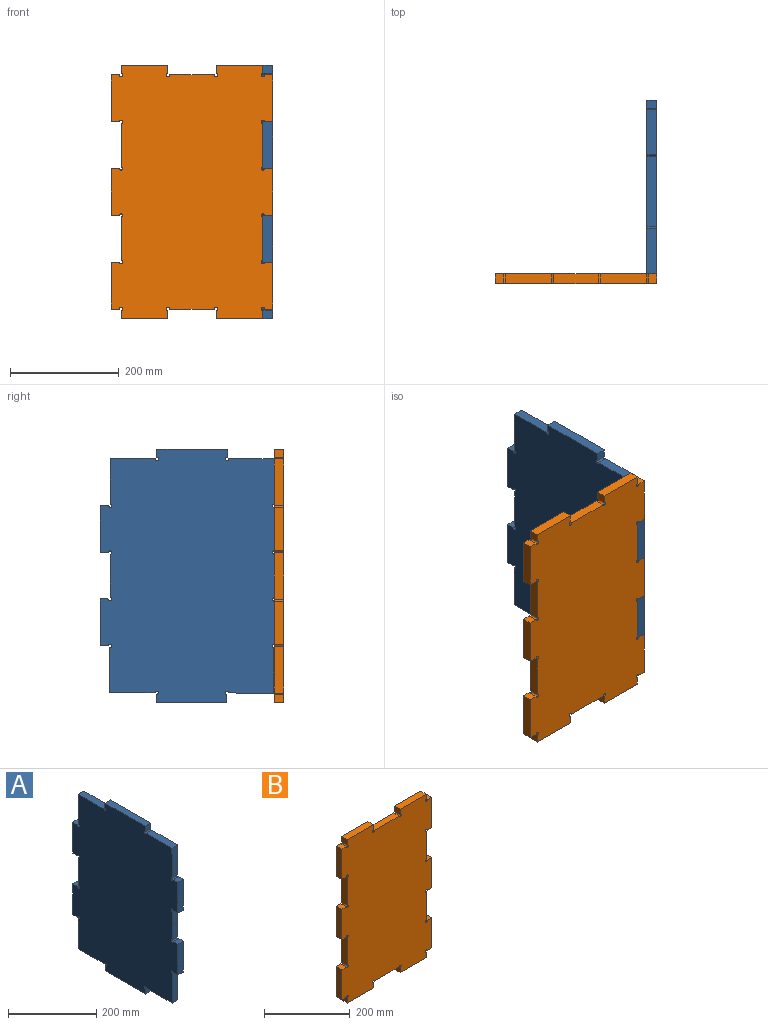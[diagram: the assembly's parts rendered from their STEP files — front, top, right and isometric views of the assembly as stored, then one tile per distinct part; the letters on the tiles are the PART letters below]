
ASSEMBLY  parts=2 mates=1
PART A: 44 faces, bbox 18x337.3x465.8 mm
  f0: plane 18x15mm, normal (0,0,1), area 270mm2, adj f24,f30,f31,f35
  f1: plane 39.62x18mm, normal (0,1,0), area 713.2mm2, adj f2,f24,f31,f35
  f2: plane 39.62x18mm, normal (0,1,0), area 713.2mm2, adj f1,f24,f31,f36
  f3: plane 18x15mm, normal (0,0,-1), area 270mm2, adj f24,f25,f31,f36
  f4: plane 18x15mm, normal (0,0,1), area 270mm2, adj f24,f25,f31,f37
  f5: plane 83x18mm, normal (0,1,0), area 1494mm2, adj f6,f24,f31,f37
  f6: plane 83x18mm, normal (0,0,1), area 1494mm2, adj f5,f24,f31,f38
  f7: plane 18x15mm, normal (0,1,0), area 270mm2, adj f24,f26,f31,f38
  f8: plane 18x15mm, normal (0,-1,0), area 270mm2, adj f24,f26,f31,f32
  f9: plane 83x18mm, normal (0,0,1), area 1494mm2, adj f10,f24,f31,f32
  f10: plane 83x18mm, normal (0,-1,0), area 1494mm2, adj f9,f24,f31,f43
  f11: plane 18x15mm, normal (0,0,1), area 270mm2, adj f24,f27,f31,f43
  f12: plane 18x15mm, normal (0,0,-1), area 270mm2, adj f24,f27,f31,f42
  f13: plane 40x18mm, normal (0,-1,0), area 720mm2, adj f14,f24,f31,f42
  f14: plane 40x18mm, normal (0,-1,0), area 720mm2, adj f13,f24,f31,f41
  f15: plane 18x15mm, normal (0,0,1), area 270mm2, adj f24,f28,f31,f41
  f16: plane 18x15mm, normal (0,0,-1), area 270mm2, adj f24,f28,f31,f40
  f17: plane 83x18mm, normal (0,-1,0), area 1494mm2, adj f18,f24,f31,f40
  f18: plane 83x18mm, normal (0,0,-1), area 1494mm2, adj f17,f24,f31,f39
  f19: plane 18x15mm, normal (0,-1,0), area 270mm2, adj f24,f29,f31,f39
  f20: plane 18x15mm, normal (0,1,0), area 270mm2, adj f24,f29,f31,f33
  f21: plane 83x18mm, normal (0,0,-1), area 1494mm2, adj f22,f24,f31,f33
  f22: plane 83x18mm, normal (0,1,0), area 1494mm2, adj f21,f24,f31,f34
  f23: plane 18x15mm, normal (0,0,-1), area 270mm2, adj f24,f30,f31,f34
  f24: plane 465.78x337.32mm, normal (1,0,0), area 139897.5mm2, adj f0,f1,f2,f3,f4,f5,f6,f7
  f25: plane 86x18mm, normal (0,1,0), area 1548mm2, adj f3,f4,f24,f31
  f26: plane 129x18mm, normal (0,0,1), area 2322mm2, adj f7,f8,f24,f31
  f27: plane 86x18mm, normal (0,-1,0), area 1548mm2, adj f11,f12,f24,f31
  f28: plane 86x18mm, normal (0,-1,0), area 1548mm2, adj f15,f16,f24,f31
  f29: plane 129x18mm, normal (0,0,-1), area 2322mm2, adj f19,f20,f24,f31
  f30: plane 86x18mm, normal (0,1,0), area 1548mm2, adj f0,f23,f24,f31
  f31: plane 465.78x337.32mm, normal (-1,0,0), area 139897.5mm2, adj f0,f1,f2,f3,f4,f5,f6,f7
  f32: cylinder r=3mm len=18mm, axis (1,0,0), area 254.5mm2, adj f8,f9,f24,f31
  f33: cylinder r=3mm len=18mm, axis (1,0,0), area 254.5mm2, adj f20,f21,f24,f31
  f34: cylinder r=3mm len=18mm, axis (1,0,0), area 254.5mm2, adj f22,f23,f24,f31
  f35: cylinder r=3mm len=18mm, axis (1,0,0), area 254.5mm2, adj f0,f1,f24,f31
  f36: cylinder r=3mm len=18mm, axis (1,0,0), area 254.5mm2, adj f2,f3,f24,f31
  f37: cylinder r=3mm len=18mm, axis (1,0,0), area 254.5mm2, adj f4,f5,f24,f31
  f38: cylinder r=3mm len=18mm, axis (1,0,0), area 254.5mm2, adj f6,f7,f24,f31
  f39: cylinder r=3mm len=18mm, axis (1,0,0), area 254.5mm2, adj f18,f19,f24,f31
  f40: cylinder r=3mm len=18mm, axis (1,0,0), area 254.5mm2, adj f16,f17,f24,f31
  f41: cylinder r=3mm len=18mm, axis (1,0,0), area 254.5mm2, adj f14,f15,f24,f31
  f42: cylinder r=3mm len=18mm, axis (1,0,0), area 254.5mm2, adj f12,f13,f24,f31
  f43: cylinder r=3mm len=18mm, axis (1,0,0), area 254.5mm2, adj f10,f11,f24,f31
PART B: 54 faces, bbox 296.2x18x466 mm
  f0: plane 82.2x18mm, normal (0,0,-1), area 1479.5mm2, adj f2,f37,f40,f48
  f1: plane 82.2x18mm, normal (0,0,1), area 1479.5mm2, adj f2,f37,f39,f47
  f2: plane 466x296.2mm, normal (0,-1,0), area 127025.4mm2, adj f0,f1,f3,f4,f5,f6,f7,f8
  f3: plane 18x15mm, normal (-1,0,0), area 269.9mm2, adj f2,f27,f37,f48
  f4: plane 18x15mm, normal (1,0,0), area 270mm2, adj f2,f27,f37,f49
  f5: plane 18x15mm, normal (0,0,-1), area 270mm2, adj f2,f28,f37,f49
  f6: plane 18x15mm, normal (0,0,1), area 270mm2, adj f2,f28,f37,f50
  f7: plane 80x18mm, normal (1,0,0), area 1440mm2, adj f2,f37,f50,f51
  f8: plane 18x15mm, normal (0,0,-1), area 270mm2, adj f2,f29,f37,f51
  f9: plane 18x15mm, normal (0,0,1), area 270mm2, adj f2,f29,f37,f52
  f10: plane 80x18mm, normal (1,0,0), area 1440mm2, adj f2,f37,f52,f53
  f11: plane 18x15mm, normal (0,0,-1), area 270mm2, adj f2,f30,f37,f53
  f12: plane 18x15mm, normal (0,0,1), area 270mm2, adj f2,f30,f37,f46
  f13: plane 18x15mm, normal (1,0,0), area 270mm2, adj f2,f31,f37,f46
  f14: plane 18x15mm, normal (-1,0,0), area 269.9mm2, adj f2,f31,f37,f47
  f15: plane 18x15mm, normal (1,0,0), area 269.9mm2, adj f2,f32,f37,f39
  f16: plane 18x15mm, normal (-1,0,0), area 270mm2, adj f2,f32,f37,f38
  f17: plane 18x15mm, normal (0,0,1), area 270mm2, adj f2,f33,f37,f38
  f18: plane 18x15mm, normal (0,0,-1), area 270mm2, adj f2,f33,f37,f45
  f19: plane 80x18mm, normal (-1,0,0), area 1440mm2, adj f2,f37,f44,f45
  f20: plane 18x15mm, normal (0,0,1), area 270mm2, adj f2,f34,f37,f44
  f21: plane 18x15mm, normal (0,0,-1), area 270mm2, adj f2,f34,f37,f43
  f22: plane 80x18mm, normal (-1,0,0), area 1440mm2, adj f2,f37,f42,f43
  f23: plane 18x15mm, normal (0,0,1), area 270mm2, adj f2,f35,f37,f42
  f24: plane 18x15mm, normal (0,0,-1), area 270mm2, adj f2,f35,f37,f41
  f25: plane 18x15mm, normal (-1,0,0), area 270mm2, adj f2,f36,f37,f41
  f26: plane 18x15mm, normal (1,0,0), area 269.9mm2, adj f2,f36,f37,f40
  f27: plane 86x18mm, normal (0,0,-1), area 1548mm2, adj f2,f3,f4,f37
  f28: plane 86x18mm, normal (1,0,0), area 1548mm2, adj f2,f5,f6,f37
  f29: plane 86x18mm, normal (1,0,0), area 1548mm2, adj f2,f8,f9,f37
  f30: plane 86x18mm, normal (1,0,0), area 1548mm2, adj f2,f11,f12,f37
  f31: plane 86x18mm, normal (0,0,1), area 1548mm2, adj f2,f13,f14,f37
  f32: plane 86x18mm, normal (0,0,1), area 1548mm2, adj f2,f15,f16,f37
  f33: plane 86x18mm, normal (-1,0,0), area 1548mm2, adj f2,f17,f18,f37
  f34: plane 86x18mm, normal (-1,0,0), area 1548mm2, adj f2,f20,f21,f37
  f35: plane 86x18mm, normal (-1,0,0), area 1548mm2, adj f2,f23,f24,f37
  f36: plane 86x18mm, normal (0,0,-1), area 1548mm2, adj f2,f25,f26,f37
  f37: plane 466x296.2mm, normal (0,1,0), area 127025.4mm2, adj f0,f1,f3,f4,f5,f6,f7,f8
  f38: cylinder r=3mm len=18mm, axis (0,-1,0), area 254.5mm2, adj f2,f16,f17,f37
  f39: cylinder r=3mm len=18mm, axis (0,-1,0), area 254.5mm2, adj f1,f2,f15,f37
  f40: cylinder r=3mm len=18mm, axis (0,-1,0), area 254.5mm2, adj f0,f2,f26,f37
  f41: cylinder r=3mm len=18mm, axis (0,-1,0), area 254.5mm2, adj f2,f24,f25,f37
  f42: cylinder r=3mm len=18mm, axis (0,-1,0), area 254.5mm2, adj f2,f22,f23,f37
  f43: cylinder r=3mm len=18mm, axis (0,-1,0), area 254.5mm2, adj f2,f21,f22,f37
  f44: cylinder r=3mm len=18mm, axis (0,-1,0), area 254.5mm2, adj f2,f19,f20,f37
  f45: cylinder r=3mm len=18mm, axis (0,-1,0), area 254.5mm2, adj f2,f18,f19,f37
  f46: cylinder r=3mm len=18mm, axis (0,-1,0), area 254.5mm2, adj f2,f12,f13,f37
  f47: cylinder r=3mm len=18mm, axis (0,-1,0), area 254.5mm2, adj f1,f2,f14,f37
  f48: cylinder r=3mm len=18mm, axis (0,-1,0), area 254.5mm2, adj f0,f2,f3,f37
  f49: cylinder r=3mm len=18mm, axis (0,-1,0), area 254.5mm2, adj f2,f4,f5,f37
  f50: cylinder r=3mm len=18mm, axis (0,-1,0), area 254.5mm2, adj f2,f6,f7,f37
  f51: cylinder r=3mm len=18mm, axis (0,-1,0), area 254.5mm2, adj f2,f7,f8,f37
  f52: cylinder r=3mm len=18mm, axis (0,-1,0), area 254.5mm2, adj f2,f9,f10,f37
  f53: cylinder r=3mm len=18mm, axis (0,-1,0), area 254.5mm2, adj f2,f10,f11,f37
PLACE A rot(axis=(1,0,0),0.1deg) t=(105.18,-190.28,20.74)mm
PLACE B t=(-24.92,-356.23,100.94)mm
MATE fastened A.f10 <-> B.f37  axis (0,-1,0) through (123.18,-356.23,315.94)mm
